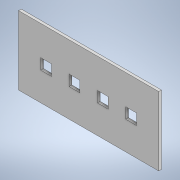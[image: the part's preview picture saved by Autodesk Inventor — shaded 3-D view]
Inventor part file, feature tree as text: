
AUTODESK INVENTOR PART (.ipt)
format: ipt  version: 2020.2 (Build 242310000, 310)  size: 122,880 bytes
history: native  units: mm
features: extrude x1, sketch x1
ambient origin geometry x8: Origin, YZ Plane, XZ Plane, XY Plane, X Axis, Y Axis, Z Axis, Center Point
bodies: Solide1 (feature_tree)
feature tree (2):
  extrude  "Extrusion1"  Depth=51.0mm
  sketch  "Esquisse1"
